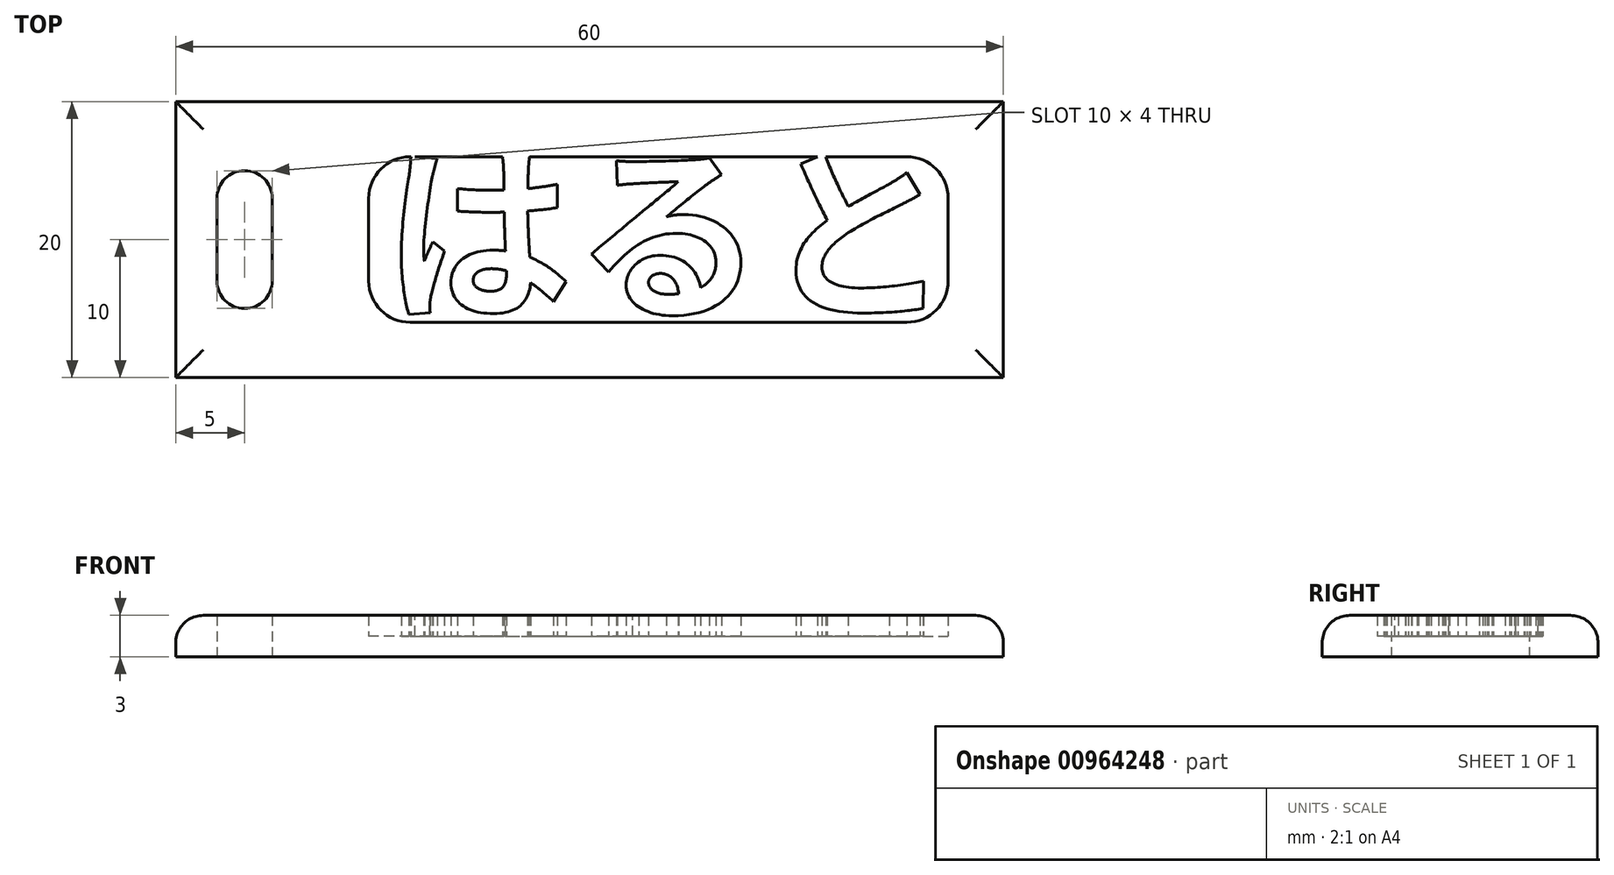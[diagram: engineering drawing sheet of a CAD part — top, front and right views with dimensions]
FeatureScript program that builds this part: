
annotation { "Feature Type Name" : "Feature", "Feature Type Description" : "" }
export const myFeature = defineFeature(function(context is Context, id is Id, definition is map)
    precondition{}
    {
        {
            var Q0;
            Q0=qCreatedBy(makeId("Top.planeOp"),FACE);
            var sketch = newSketch(context, id + "F0", { "sketchPlane" : qUnion([Q0])});
            skLineSegment(sketch, "E0.bottom", {"start": v(-25, 10) * mm, "end": v(25, 10) * mm});
            skLineSegment(sketch, "E0.top", {"start": v(-25, -10) * mm, "end": v(25, -10) * mm});
            skLineSegment(sketch, "E0.left", {"start": v(-25, 10) * mm, "end": v(-25, -10) * mm});
            skLineSegment(sketch, "E0.right", {"start": v(25, 10) * mm, "end": v(25, -10) * mm});
            skPoint(sketch, "E0.middle", {"position": v(0, 0) * mm});
            skLineSegment(sketch, "E1.bottom", {"start": v(-25, 10) * mm, "end": v(-35, 10) * mm});
            skLineSegment(sketch, "E1.top", {"start": v(-25, -10) * mm, "end": v(-35, -10) * mm});
            skLineSegment(sketch, "E1.right", {"start": v(-35, 10) * mm, "end": v(-35, -10) * mm});
            skPoint(sketch, "E1.middle", {"position": v(-30, 0) * mm});
            skPoint(sketch, "E1.middle.positionSnap0", {"position": v(-25, 0) * mm});
            skPoint(sketch, "E1.centerSnap0", {"position": v(-25, 0) * mm});
            skLineSegment(sketch, "E2.bottom", {"start": v(-30, 5) * mm, "end": v(-30, 5) * mm});
            skLineSegment(sketch, "E2.top", {"start": v(-30, -5) * mm, "end": v(-30, -5) * mm});
            skLineSegment(sketch, "E2.left", {"start": v(-32, 3) * mm, "end": v(-32, -3) * mm});
            skLineSegment(sketch, "E2.right", {"start": v(-28, 3) * mm, "end": v(-28, -3) * mm});
            skPoint(sketch, "E3.visualSharp", {"position": v(-32, 5) * mm});
            skArc(sketch, "E3.filletArc", {"start": v(-30, 5) * mm, "mid": v(-31.41, 4.41) * mm, "end": v(-32, 3) * mm});
            skPoint(sketch, "E4.visualSharp", {"position": v(-28, 5) * mm});
            skArc(sketch, "E4.filletArc", {"start": v(-28, 3) * mm, "mid": v(-28.59, 4.41) * mm, "end": v(-30, 5) * mm});
            skPoint(sketch, "E5.visualSharp", {"position": v(-28, -5) * mm});
            skArc(sketch, "E5.filletArc", {"start": v(-30, -5) * mm, "mid": v(-28.59, -4.41) * mm, "end": v(-28, -3) * mm});
            skPoint(sketch, "E6.visualSharp", {"position": v(-32, -5) * mm});
            skArc(sketch, "E6.filletArc", {"start": v(-32, -3) * mm, "mid": v(-31.41, -4.41) * mm, "end": v(-30, -5) * mm});
            skSolve(sketch);
        }
        {
            var Q0;
            Q0=qSketchRegion(id+"F0",true);
            extrude(context, id + "F1", {"entities" : qUnion([Q0]), "depth" : 3 * mm, "offsetDistance" : 25 * mm});
        }
        {
            var Q0;
            Q0=qCreatedBy(makeId("Top.planeOp"),FACE);
            var sketch = newSketch(context, id + "F2", { "sketchPlane" : qUnion([Q0])});
            skLineSegment(sketch, "E7.bottom", {"start": v(-18, 6) * mm, "end": v(18, 6) * mm});
            skLineSegment(sketch, "E7.top", {"start": v(-18, -6) * mm, "end": v(18, -6) * mm});
            skLineSegment(sketch, "E7.left", {"start": v(-21, 3) * mm, "end": v(-21, -3) * mm});
            skLineSegment(sketch, "E7.right", {"start": v(21, 3) * mm, "end": v(21, -3) * mm});
            skPoint(sketch, "E7.middle", {"position": v(0, 0) * mm});
            skPoint(sketch, "E8.visualSharp", {"position": v(-21, 6) * mm});
            skArc(sketch, "E8.filletArc", {"start": v(-18, 6) * mm, "mid": v(-20.12, 5.12) * mm, "end": v(-21, 3) * mm});
            skPoint(sketch, "E9.visualSharp", {"position": v(21, 6) * mm});
            skArc(sketch, "E9.filletArc", {"start": v(21, 3) * mm, "mid": v(20.12, 5.12) * mm, "end": v(18, 6) * mm});
            skPoint(sketch, "E10.visualSharp", {"position": v(21, -6) * mm});
            skArc(sketch, "E10.filletArc", {"start": v(18, -6) * mm, "mid": v(20.12, -5.12) * mm, "end": v(21, -3) * mm});
            skPoint(sketch, "E11.visualSharp", {"position": v(-21, -6) * mm});
            skArc(sketch, "E11.filletArc", {"start": v(-21, -3) * mm, "mid": v(-20.12, -5.12) * mm, "end": v(-18, -6) * mm});
            skSolve(sketch);
        }
        {
            var Q0;
            Q0=qSketchRegion(id+"F2",true);
            extrude(context, id + "F3", {"entities" : qUnion([Q0]), "depth" : 3 * mm, "offsetDistance" : 25 * mm});
        }
        {
            var Q0;
            Q0=makeQuery(id+"F3.opExtrude","SWEPT_BODY",BODY,{"disambiguationData":[OSD([sQuery(id+"F2.wireOp",EDGE,"E7.bottom"),sQuery(id+"F2.wireOp",EDGE,"E7.top"),sQuery(id+"F2.wireOp",EDGE,"E7.left"),sQuery(id+"F2.wireOp",EDGE,"E7.right"),sQuery(id+"F2.wireOp",EDGE,"E8.filletArc"),sQuery(id+"F2.wireOp",EDGE,"E9.filletArc"),sQuery(id+"F2.wireOp",EDGE,"E10.filletArc"),sQuery(id+"F2.wireOp",EDGE,"E11.filletArc")])]});
            transform(context, id + "F4", {"entities" : qUnion([Q0]), "transformType" : TransformType.TRANSLATION_3D, "dx" : 0 * mm, "dy" : 0 * mm, "dz" : 1.5 * mm, "makeCopy" : false});
        }
        {
            var Q0;
            Q0=makeQuery(id+"F3.opExtrude","SWEPT_BODY",BODY,{"disambiguationData":[OSD([sQuery(id+"F2.wireOp",EDGE,"E7.bottom"),sQuery(id+"F2.wireOp",EDGE,"E7.top"),sQuery(id+"F2.wireOp",EDGE,"E7.left"),sQuery(id+"F2.wireOp",EDGE,"E7.right"),sQuery(id+"F2.wireOp",EDGE,"E8.filletArc"),sQuery(id+"F2.wireOp",EDGE,"E9.filletArc"),sQuery(id+"F2.wireOp",EDGE,"E10.filletArc"),sQuery(id+"F2.wireOp",EDGE,"E11.filletArc")])]});
            var Q1;
            Q1=makeQuery(id+"F1.opExtrude","SWEPT_BODY",BODY,{"disambiguationData":[OSD([sQuery(id+"F0.wireOp",EDGE,"E0.bottom"),sQuery(id+"F0.wireOp",EDGE,"E0.top"),sQuery(id+"F0.wireOp",EDGE,"E0.right"),sQuery(id+"F0.wireOp",EDGE,"E1.bottom"),sQuery(id+"F0.wireOp",EDGE,"E1.top"),sQuery(id+"F0.wireOp",EDGE,"E1.right"),sQuery(id+"F0.wireOp",EDGE,"E2.left"),sQuery(id+"F0.wireOp",EDGE,"E2.right"),sQuery(id+"F0.wireOp",EDGE,"E3.filletArc"),sQuery(id+"F0.wireOp",EDGE,"E4.filletArc"),sQuery(id+"F0.wireOp",EDGE,"E5.filletArc"),sQuery(id+"F0.wireOp",EDGE,"E6.filletArc")])]});
            booleanBodies(context, id + "F5", {"operationType" : BooleanOperationType.SUBTRACTION, "tools" : qUnion([Q0]), "targets" : qUnion([Q1])});
        }
        {
            var Q0;
            Q0=qCreatedBy(makeId("Top.planeOp"),FACE);
            var sketch = newSketch(context, id + "F6", { "sketchPlane" : qUnion([Q0])});
            skText(sketch, "E12", { "text": "はると", "fontName": "NotoSansCJKjp-Bold.otf"});
            const initialGuessF6  = {"E12": [-0.02, -0.0048, 1, 0, 0.00998]};
            skSetInitialGuess(sketch, initialGuessF6);
            skSolve(sketch);
        }
        {
            var Q0;
            Q0 = qSketchRegion(id + "F6", true);
            extrude(context, id + "F7", {"entities" : qUnion([Q0]), "operationType" : NewBodyOperationType.ADD, "depth" : 3 * mm, "offsetDistance" : 25 * mm});
        }
        {
            var Q0;
            Q0=makeQuery(id+"F1.opExtrude","CAP_EDGE",EDGE,{"disambiguationData":[OSD([sQuery(id+"F0.wireOp",EDGE,"E0.bottom"),sQuery(id+"F0.wireOp",EDGE,"E1.bottom")])],"isStart":false});
            var Q1;
            Q1=makeQuery(id+"F1.opExtrude","CAP_EDGE",EDGE,{"disambiguationData":[OSD([sQuery(id+"F0.wireOp",EDGE,"E1.right")])],"isStart":false});
            var Q2;
            Q2=makeQuery(id+"F1.opExtrude","CAP_EDGE",EDGE,{"disambiguationData":[OSD([sQuery(id+"F0.wireOp",EDGE,"E0.top"),sQuery(id+"F0.wireOp",EDGE,"E1.top")])],"isStart":false});
            var Q3;
            Q3=makeQuery(id+"F1.opExtrude","CAP_EDGE",EDGE,{"disambiguationData":[OSD([sQuery(id+"F0.wireOp",EDGE,"E0.right")])],"isStart":false});
            fillet(context, id + "F8", {"entities" : qUnion([Q0, Q1, Q2, Q3]), "radius" : 2 * mm, "tangentPropagation" : true, "allowEdgeOverflow" : false});
        }
    });
